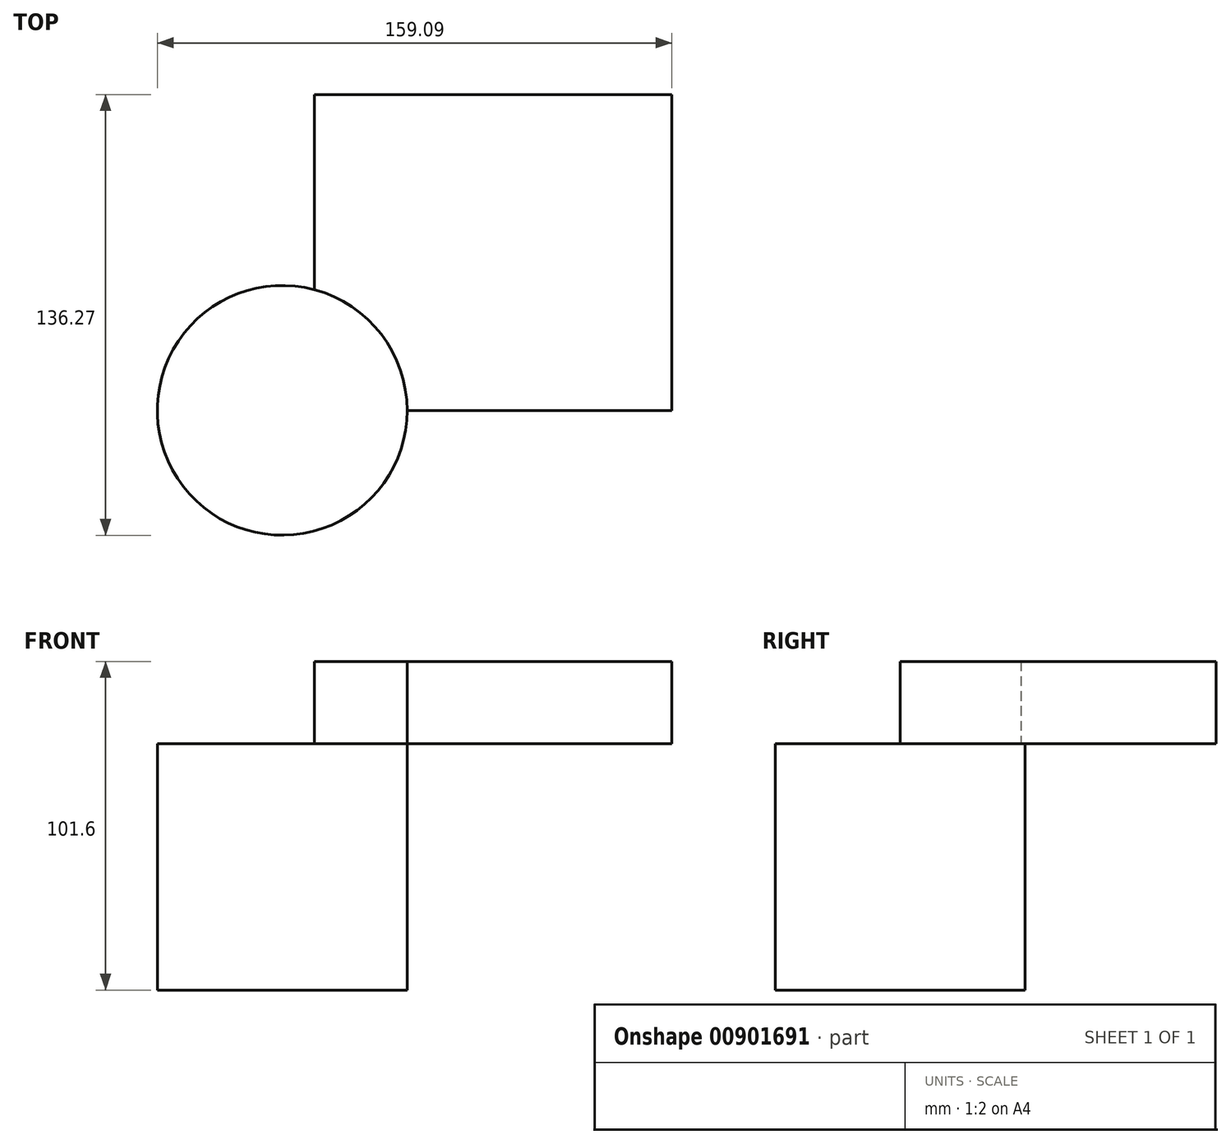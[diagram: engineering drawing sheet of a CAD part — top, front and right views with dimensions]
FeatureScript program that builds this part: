
annotation { "Feature Type Name" : "Feature", "Feature Type Description" : "" }
export const myFeature = defineFeature(function(context is Context, id is Id, definition is map)
    precondition{}
    {
        {
            var Q0;
            Q0=qCreatedBy(makeId("Top.planeOp"),FACE);
            var sketch = newSketch(context, id + "F0", { "sketchPlane" : qUnion([Q0])});
            skCircle(sketch, "E0", {"center": v(0, 0) * mm, "radius": 38.6 * mm});
            skSolve(sketch);
        }
        {
            var Q0;
            Q0=makeQuery(id+"F0.imprint","IMPRINT",FACE,{"disambiguationData":[TD([[makeQuery(id+"F0.imprint","IMPRINT",EDGE,{"derivedFrom":sQuery(id+"F0.wireOp",EDGE,"E0")}),1.0]])]});
            extrude(context, id + "F1", {"entities" : qUnion([Q0]), "depth" : 76.2 * mm, "offsetDistance" : 25.4 * mm});
        }
        {
            var Q0;
            Q0=makeQuery(id+"F1.opExtrude","CAP_FACE",FACE,{"disambiguationData":[OSD([sQuery(id+"F0.wireOp",EDGE,"E0")])],"isStart":false});
            var sketch = newSketch(context, id + "F2", { "sketchPlane" : qUnion([Q0])});
            skLineSegment(sketch, "E1.bottom", {"start": v(9.96, 0) * mm, "end": v(120.48, 0) * mm});
            skLineSegment(sketch, "E1.top", {"start": v(9.96, 97.66) * mm, "end": v(120.48, 97.66) * mm});
            skLineSegment(sketch, "E1.left", {"start": v(9.96, 0) * mm, "end": v(9.96, 97.66) * mm});
            skLineSegment(sketch, "E1.right", {"start": v(120.48, 0) * mm, "end": v(120.48, 97.66) * mm});
            skSolve(sketch);
        }
        {
            var Q0;
            {var subQ2=sQuery(id+"F2.wireOp",EDGE,"E1.top");Q0=makeQuery(id+"F2.imprint","IMPRINT",FACE,{"disambiguationData":[TD([[makeQuery(id+"F2.imprint","IMPRINT",EDGE,{"derivedFrom":subQ2}),-1.0]])]});}
            extrude(context, id + "F3", {"entities" : qUnion([Q0]), "depth" : 25.4 * mm, "offsetDistance" : 25.4 * mm});
        }
    });
